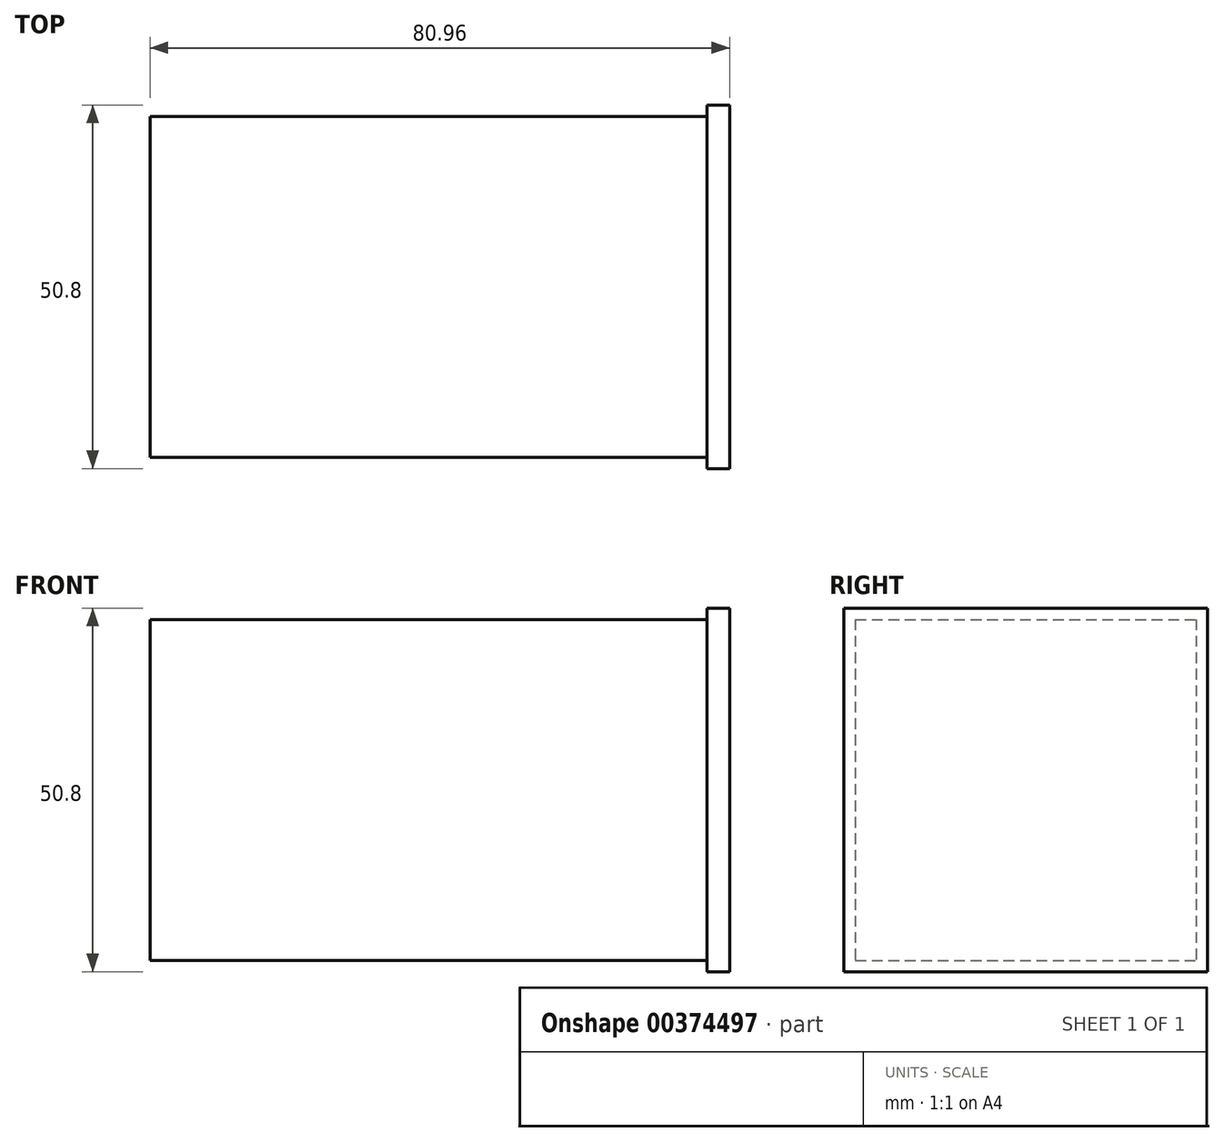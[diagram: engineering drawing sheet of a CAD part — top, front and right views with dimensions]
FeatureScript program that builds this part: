
annotation { "Feature Type Name" : "Feature", "Feature Type Description" : "" }
export const myFeature = defineFeature(function(context is Context, id is Id, definition is map)
    precondition{}
    {
        {
            var Q0;
            Q0=qCreatedBy(makeId("Right.planeOp"),FACE);
            var sketch = newSketch(context, id + "F0", { "sketchPlane" : qUnion([Q0])});
            skLineSegment(sketch, "E0.bottom", {"start": v(-23.81, 23.81) * mm, "end": v(23.81, 23.81) * mm});
            skLineSegment(sketch, "E0.top", {"start": v(-23.81, -23.81) * mm, "end": v(23.81, -23.81) * mm});
            skLineSegment(sketch, "E0.left", {"start": v(-23.81, 23.81) * mm, "end": v(-23.81, -23.81) * mm});
            skLineSegment(sketch, "E0.right", {"start": v(23.81, 23.81) * mm, "end": v(23.81, -23.81) * mm});
            skSolve(sketch);
        }
        {
            var Q0;
            Q0=makeQuery(id+"F0.imprint","IMPRINT",FACE,{"disambiguationData":[TD([[makeQuery(id+"F0.imprint","IMPRINT",EDGE,{"derivedFrom":sQuery(id+"F0.wireOp",EDGE,"E0.bottom")}),-1.0]])]});
            extrude(context, id + "F1", {"entities" : qUnion([Q0]), "depth" : 77.8 * mm});
        }
        {
            var Q0;
            Q0=makeQuery(id+"F1.opExtrude","CAP_FACE",FACE,{"disambiguationData":[OSD([sQuery(id+"F0.wireOp",EDGE,"E0.bottom"),sQuery(id+"F0.wireOp",EDGE,"E0.top"),sQuery(id+"F0.wireOp",EDGE,"E0.left"),sQuery(id+"F0.wireOp",EDGE,"E0.right")])],"isStart":false});
            var sketch = newSketch(context, id + "F2", { "sketchPlane" : qUnion([Q0])});
            skLineSegment(sketch, "E1.bottom", {"start": v(-25.4, 25.4) * mm, "end": v(25.4, 25.4) * mm});
            skLineSegment(sketch, "E1.top", {"start": v(-25.4, -25.4) * mm, "end": v(25.4, -25.4) * mm});
            skLineSegment(sketch, "E1.left", {"start": v(-25.4, 25.4) * mm, "end": v(-25.4, -25.4) * mm});
            skLineSegment(sketch, "E1.right", {"start": v(25.4, 25.4) * mm, "end": v(25.4, -25.4) * mm});
            skPoint(sketch, "E1.middle", {"position": v(0, 0) * mm});
            skSolve(sketch);
        }
        {
            var Q0;
            Q0 = qSketchRegion(id + "F2", true);
            extrude(context, id + "F3", {"entities" : qUnion([Q0]), "operationType" : NewBodyOperationType.ADD, "depth" : 3.17 * mm});
        }
    });
